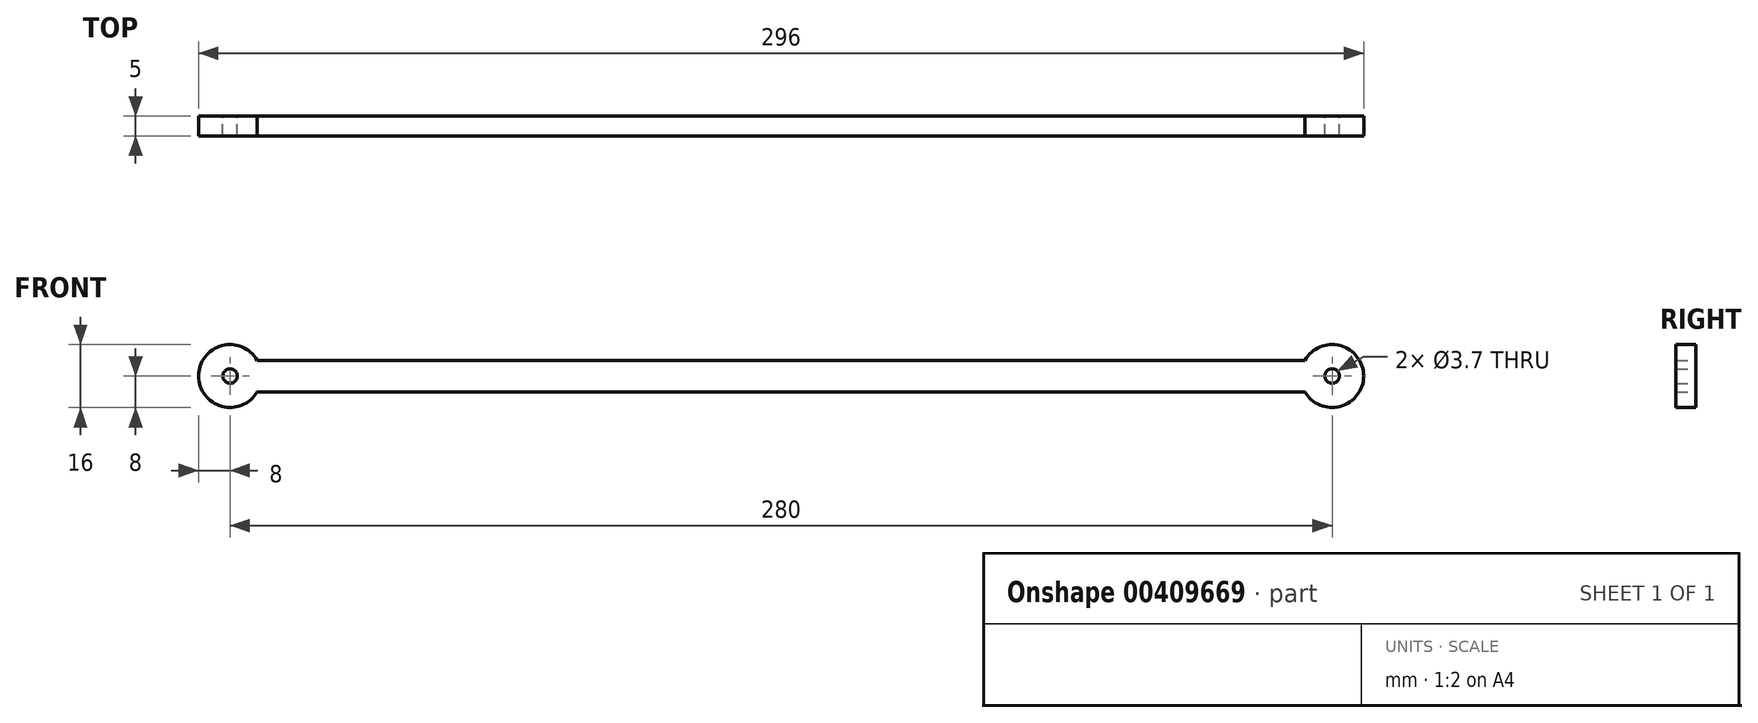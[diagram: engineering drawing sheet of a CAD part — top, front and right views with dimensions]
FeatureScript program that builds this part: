
annotation { "Feature Type Name" : "Feature", "Feature Type Description" : "" }
export const myFeature = defineFeature(function(context is Context, id is Id, definition is map)
    precondition{}
    {
        {
            var Q0;
            Q0=qCreatedBy(makeId("Front.planeOp"),FACE);
            var sketch = newSketch(context, id + "F0", { "sketchPlane" : qUnion([Q0])});
            skCircle(sketch, "E0", {"center": v(-140, 0) * mm, "radius": 1.85 * mm});
            skCircle(sketch, "E1", {"center": v(140, 0) * mm, "radius": 1.85 * mm});
            skArc(sketch, "E2", {"start": v(-133.07, 4) * mm, "mid": v(-148, 0) * mm, "end": v(-133.07, -4) * mm});
            skArc(sketch, "E3", {"start": v(133.07, -4) * mm, "mid": v(148, 0) * mm, "end": v(133.07, 4) * mm});
            skLineSegment(sketch, "E4.bottom", {"start": v(133.07, -4) * mm, "end": v(-133.07, -4) * mm});
            skLineSegment(sketch, "E4.top", {"start": v(133.07, 4) * mm, "end": v(-133.07, 4) * mm});
            skPoint(sketch, "E4.middle", {"position": v(0, 0) * mm});
            skSolve(sketch);
        }
        {
            var Q0;
            Q0=makeQuery(id+"F0.imprint","IMPRINT",FACE,{"disambiguationData":[TD([[makeQuery(id+"F0.imprint","IMPRINT",EDGE,{"derivedFrom":sQuery(id+"F0.wireOp",EDGE,"E0")}),-1.0]])]});
            extrude(context, id + "F1", {"entities" : qUnion([Q0]), "endBound" : BoundingType.SYMMETRIC, "depth" : 5 * mm});
        }
    });
